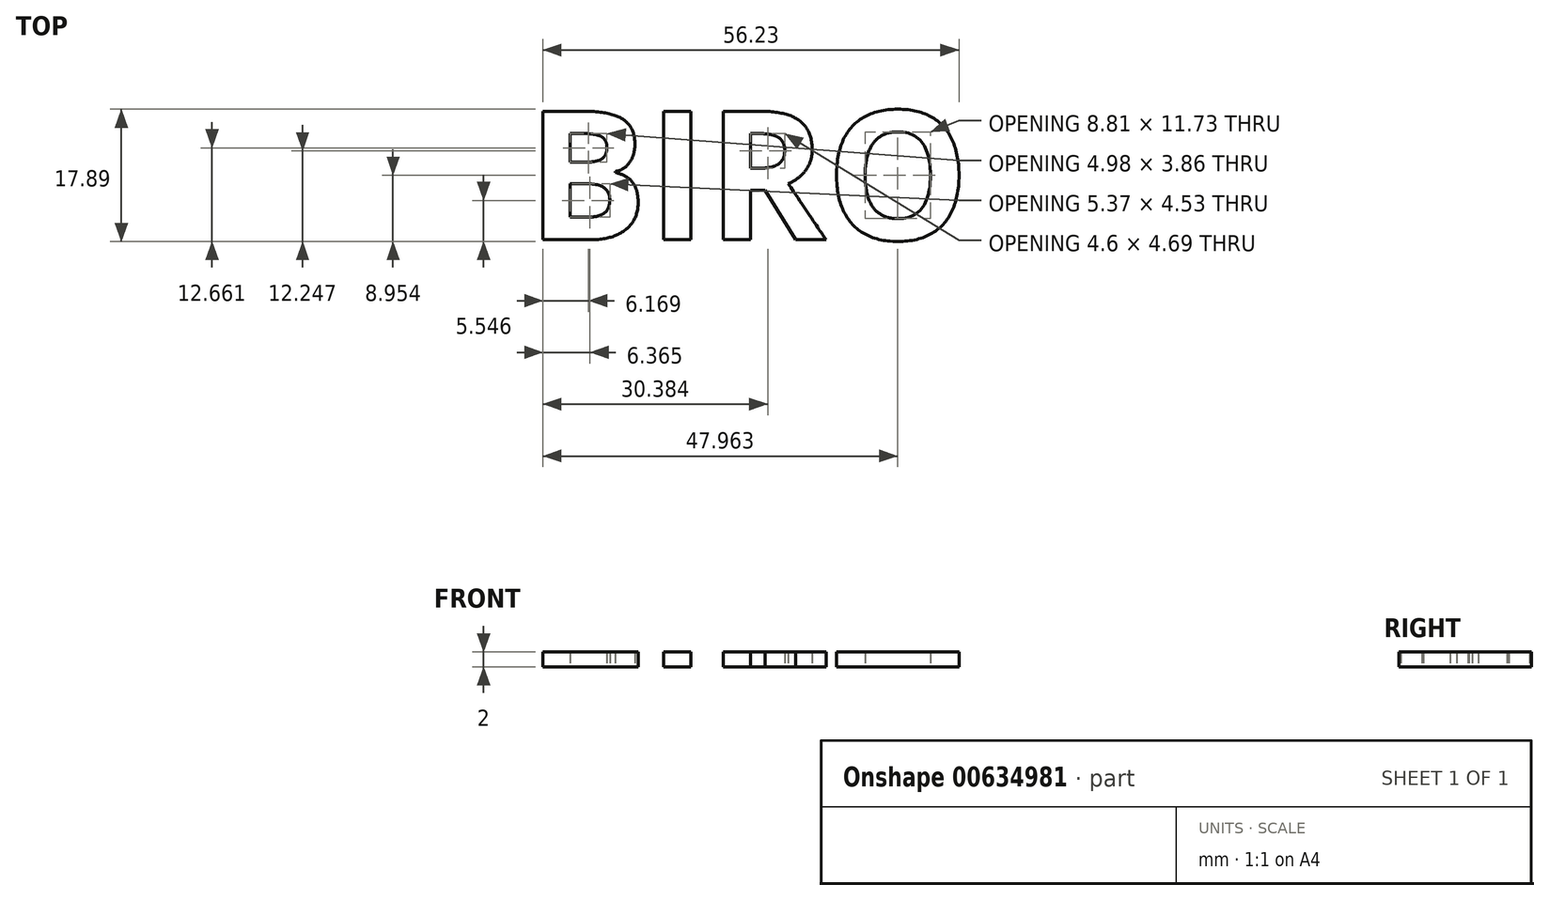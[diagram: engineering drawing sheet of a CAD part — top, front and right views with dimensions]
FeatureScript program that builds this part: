
annotation { "Feature Type Name" : "Feature", "Feature Type Description" : "" }
export const myFeature = defineFeature(function(context is Context, id is Id, definition is map)
    precondition{}
    {
        {
            var Q0;
            Q0=qCreatedBy(makeId("Top.planeOp"),FACE);
            var sketch = newSketch(context, id + "F0", { "sketchPlane" : qUnion([Q0])});
            skText(sketch, "E0", { "text": "BIRO", "fontName": "OpenSans-Bold.ttf"});
            const initialGuessF0  = {"E0": [-0.02509, -0.01175, 1, 0, 0.01752]};
            skSetInitialGuess(sketch, initialGuessF0);
            skSolve(sketch);
        }
        {
            var Q0;
            Q0 = qSketchRegion(id + "F0", true);
            extrude(context, id + "F1", {"entities" : qUnion([Q0]), "depth" : 2 * mm, "offsetDistance" : 25 * mm});
        }
    });
